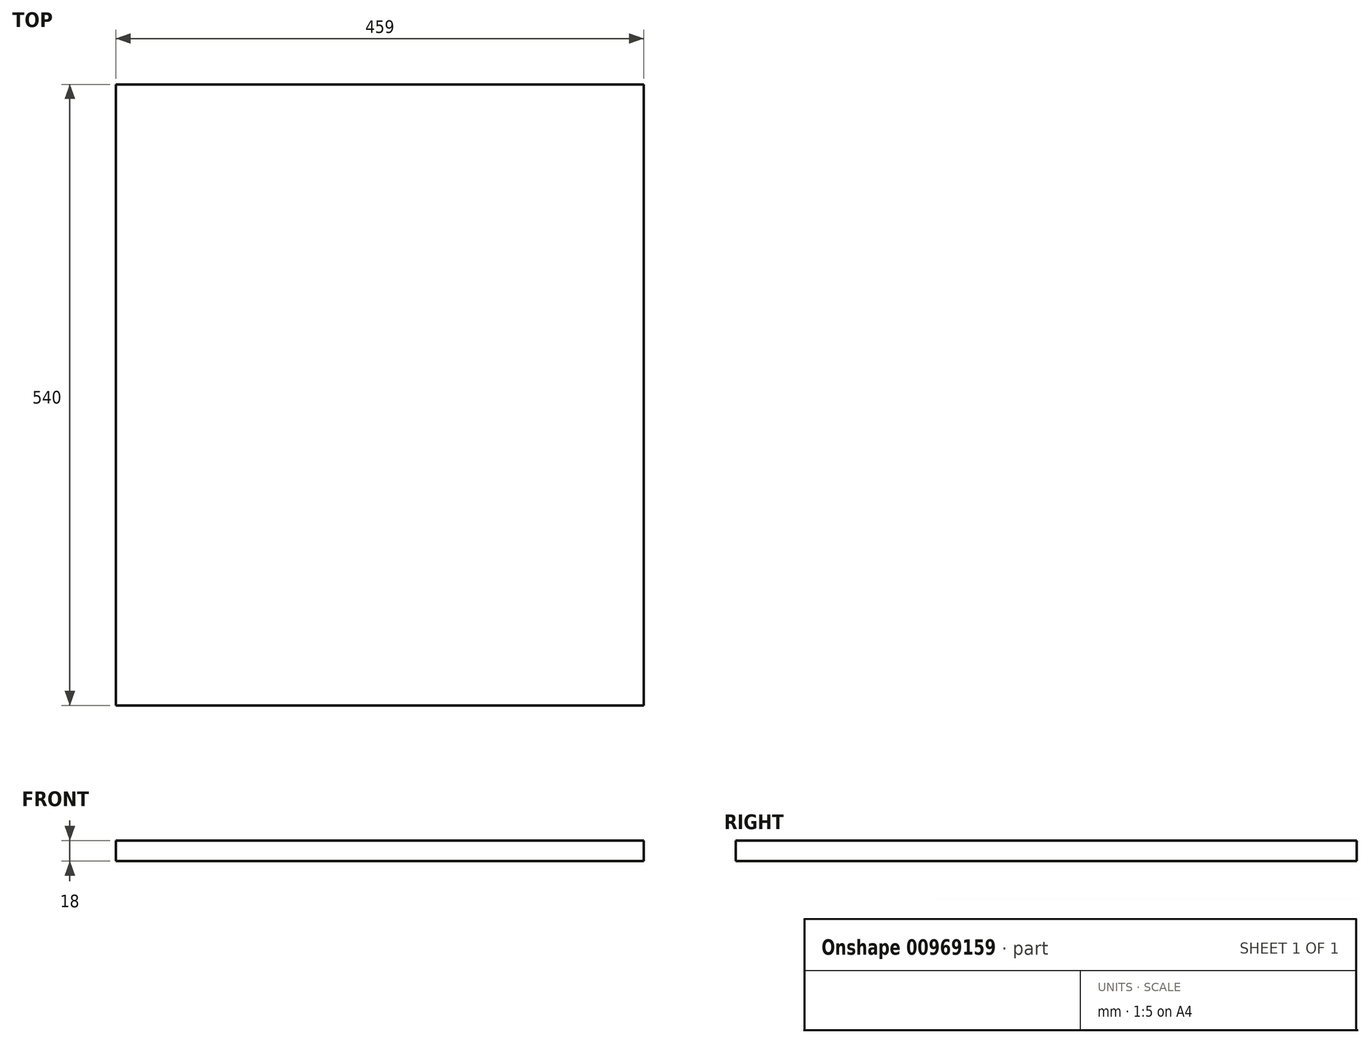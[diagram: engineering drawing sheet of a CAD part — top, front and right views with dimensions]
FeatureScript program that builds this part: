
annotation { "Feature Type Name" : "Feature", "Feature Type Description" : "" }
export const myFeature = defineFeature(function(context is Context, id is Id, definition is map)
    precondition{}
    {
        {
            var Q0;
            Q0=qCreatedBy(makeId("Top.planeOp"),FACE);
            var sketch = newSketch(context, id + "F0", { "sketchPlane" : qUnion([Q0])});
            skLineSegment(sketch, "E0.bottom", {"start": v(0, 0) * mm, "end": v(459, 0) * mm});
            skLineSegment(sketch, "E0.top", {"start": v(0, 540) * mm, "end": v(459, 540) * mm});
            skLineSegment(sketch, "E0.left", {"start": v(0, 0) * mm, "end": v(0, 540) * mm});
            skLineSegment(sketch, "E0.right", {"start": v(459, 0) * mm, "end": v(459, 540) * mm});
            skSolve(sketch);
        }
        {
            var Q0;
            Q0 = qSketchRegion(id + "F0", true);
            extrude(context, id + "F1", {"entities" : qUnion([Q0]), "depth" : 18 * mm, "offsetDistance" : 25 * mm});
        }
    });
